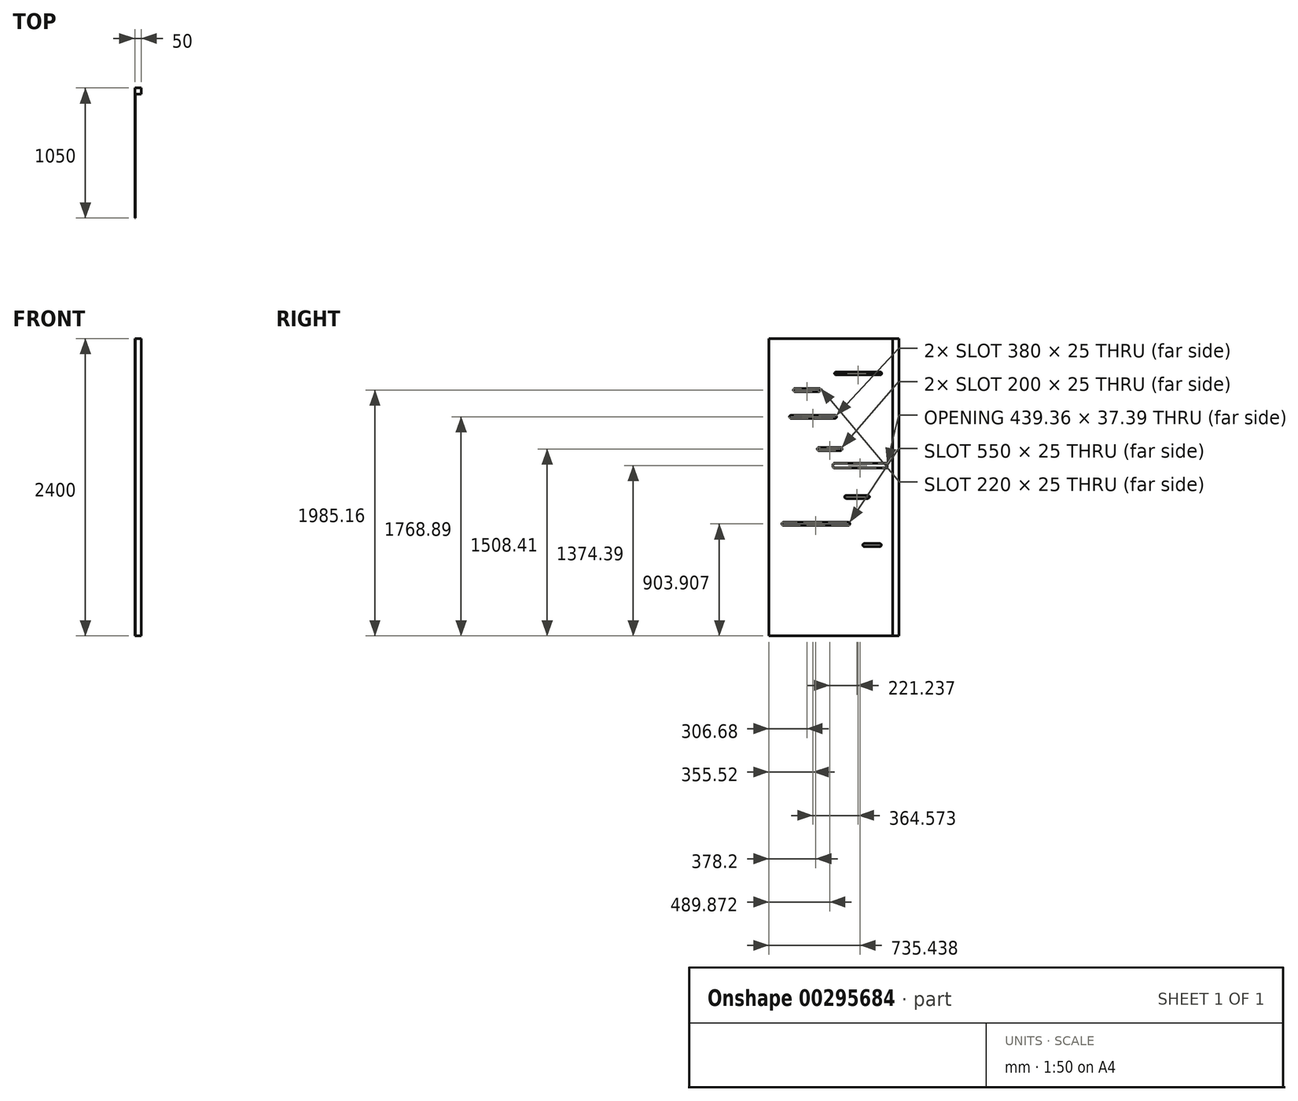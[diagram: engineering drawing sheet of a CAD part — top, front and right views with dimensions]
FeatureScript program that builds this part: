
annotation { "Feature Type Name" : "Feature", "Feature Type Description" : "" }
export const myFeature = defineFeature(function(context is Context, id is Id, definition is map)
    precondition{}
    {
        {
            var Q0;
            Q0=qCreatedBy(makeId("Top.planeOp"),FACE);
            var sketch = newSketch(context, id + "F0", { "sketchPlane" : qUnion([Q0])});
            skLineSegment(sketch, "E0.bottom", {"start": v(0, 0) * mm, "end": v(-50, 0) * mm});
            skLineSegment(sketch, "E0.top", {"start": v(0, -50) * mm, "end": v(-50, -50) * mm});
            skLineSegment(sketch, "E0.left", {"start": v(0, 0) * mm, "end": v(0, -50) * mm});
            skLineSegment(sketch, "E0.right", {"start": v(-50, 0) * mm, "end": v(-50, -50) * mm});
            skLineSegment(sketch, "E1.bottom", {"start": v(-50, -50) * mm, "end": v(-47, -50) * mm});
            skLineSegment(sketch, "E1.top", {"start": v(-50, -1050) * mm, "end": v(-47, -1050) * mm});
            skLineSegment(sketch, "E1.left", {"start": v(-50, -50) * mm, "end": v(-50, -1050) * mm});
            skLineSegment(sketch, "E1.right", {"start": v(-47, -50) * mm, "end": v(-47, -1050) * mm});
            skSolve(sketch);
        }
        {
            var Q0;
            Q0 = qSketchRegion(id + "F0", true);
            extrude(context, id + "F1", {"entities" : qUnion([Q0]), "depth" : 2400 * mm});
        }
        {
            var Q0;
            Q0=makeQuery(id+"F1.opExtrude","SWEPT_FACE",FACE,{"disambiguationData":[OSD([sQuery(id+"F0.wireOp",EDGE,"E0.right"),sQuery(id+"F0.wireOp",EDGE,"E1.left")])]});
            var sketch = newSketch(context, id + "F2", { "sketchPlane" : qUnion([Q0])});
            skLineSegment(sketch, "E2.bottom", {"start": v(152.4, 2131.65) * mm, "end": v(507.4, 2131.65) * mm});
            skLineSegment(sketch, "E2.top", {"start": v(152.4, 2106.65) * mm, "end": v(507.4, 2106.65) * mm});
            skLineSegment(sketch, "E2.left", {"start": v(139.9, 2119.15) * mm, "end": v(139.9, 2119.15) * mm});
            skLineSegment(sketch, "E2.right", {"start": v(519.9, 2119.15) * mm, "end": v(519.9, 2119.15) * mm});
            skLineSegment(sketch, "E3.bottom", {"start": v(516.98, 1781.39) * mm, "end": v(871.98, 1781.39) * mm});
            skLineSegment(sketch, "E3.top", {"start": v(516.98, 1756.39) * mm, "end": v(871.98, 1756.39) * mm});
            skLineSegment(sketch, "E3.left", {"start": v(504.48, 1768.89) * mm, "end": v(504.48, 1768.89) * mm});
            skLineSegment(sketch, "E3.right", {"start": v(884.48, 1768.89) * mm, "end": v(884.48, 1768.89) * mm});
            skLineSegment(sketch, "E4.bottom", {"start": v(472.63, 1520.91) * mm, "end": v(647.63, 1520.91) * mm});
            skLineSegment(sketch, "E4.top", {"start": v(472.63, 1495.91) * mm, "end": v(647.63, 1495.91) * mm});
            skLineSegment(sketch, "E4.left", {"start": v(460.13, 1508.41) * mm, "end": v(460.13, 1508.41) * mm});
            skLineSegment(sketch, "E4.right", {"start": v(660.13, 1508.41) * mm, "end": v(660.13, 1508.41) * mm});
            skLineSegment(sketch, "E5.bottom", {"start": v(251.4, 1134.53) * mm, "end": v(426.4, 1134.53) * mm});
            skLineSegment(sketch, "E5.top", {"start": v(251.4, 1109.53) * mm, "end": v(426.4, 1109.53) * mm});
            skLineSegment(sketch, "E5.left", {"start": v(238.9, 1122.03) * mm, "end": v(238.9, 1122.03) * mm});
            skLineSegment(sketch, "E5.right", {"start": v(438.9, 1122.03) * mm, "end": v(438.9, 1122.03) * mm});
            skLineSegment(sketch, "E6.bottom", {"start": v(409.3, 916.4) * mm, "end": v(934.3, 916.4) * mm});
            skLineSegment(sketch, "E6.top", {"start": v(409.3, 891.4) * mm, "end": v(934.3, 891.4) * mm});
            skLineSegment(sketch, "E6.left", {"start": v(396.8, 903.9) * mm, "end": v(396.8, 903.9) * mm});
            skLineSegment(sketch, "E6.right", {"start": v(946.8, 903.9) * mm, "end": v(946.8, 903.9) * mm});
            skLineSegment(sketch, "E7.bottom", {"start": v(154.94, 745.03) * mm, "end": v(279.94, 745.03) * mm});
            skLineSegment(sketch, "E7.top", {"start": v(154.94, 720.03) * mm, "end": v(279.94, 720.03) * mm});
            skLineSegment(sketch, "E7.left", {"start": v(142.44, 732.53) * mm, "end": v(142.44, 732.53) * mm});
            skLineSegment(sketch, "E7.right", {"start": v(292.44, 732.53) * mm, "end": v(292.44, 732.53) * mm});
            skLineSegment(sketch, "E8.bottom", {"start": v(645.82, 1997.66) * mm, "end": v(840.82, 1997.66) * mm});
            skLineSegment(sketch, "E8.top", {"start": v(645.82, 1972.66) * mm, "end": v(840.82, 1972.66) * mm});
            skLineSegment(sketch, "E8.left", {"start": v(633.32, 1985.16) * mm, "end": v(633.32, 1985.16) * mm});
            skLineSegment(sketch, "E8.right", {"start": v(853.32, 1985.16) * mm, "end": v(853.32, 1985.16) * mm});
            skPoint(sketch, "E9.visualSharp", {"position": v(504.48, 1781.39) * mm});
            skArc(sketch, "E9.filletArc", {"start": v(516.98, 1781.39) * mm, "mid": v(508.14, 1777.73) * mm, "end": v(504.48, 1768.89) * mm});
            skPoint(sketch, "E10.visualSharp", {"position": v(504.48, 1756.39) * mm});
            skArc(sketch, "E10.filletArc", {"start": v(504.48, 1768.89) * mm, "mid": v(508.14, 1760.05) * mm, "end": v(516.98, 1756.39) * mm});
            skPoint(sketch, "E11.visualSharp", {"position": v(884.48, 1781.39) * mm});
            skArc(sketch, "E11.filletArc", {"start": v(884.48, 1768.89) * mm, "mid": v(880.82, 1777.73) * mm, "end": v(871.98, 1781.39) * mm});
            skPoint(sketch, "E12.visualSharp", {"position": v(884.48, 1756.39) * mm});
            skArc(sketch, "E12.filletArc", {"start": v(871.98, 1756.39) * mm, "mid": v(880.82, 1760.05) * mm, "end": v(884.48, 1768.89) * mm});
            skPoint(sketch, "E13.visualSharp", {"position": v(660.13, 1520.91) * mm});
            skArc(sketch, "E13.filletArc", {"start": v(660.13, 1508.41) * mm, "mid": v(656.47, 1517.25) * mm, "end": v(647.63, 1520.91) * mm});
            skPoint(sketch, "E14.visualSharp", {"position": v(660.13, 1495.91) * mm});
            skArc(sketch, "E14.filletArc", {"start": v(647.63, 1495.91) * mm, "mid": v(656.47, 1499.57) * mm, "end": v(660.13, 1508.41) * mm});
            skPoint(sketch, "E15.visualSharp", {"position": v(460.13, 1495.91) * mm});
            skArc(sketch, "E15.filletArc", {"start": v(460.13, 1508.41) * mm, "mid": v(463.79, 1499.57) * mm, "end": v(472.63, 1495.91) * mm});
            skPoint(sketch, "E16.visualSharp", {"position": v(460.13, 1520.91) * mm});
            skArc(sketch, "E16.filletArc", {"start": v(472.63, 1520.91) * mm, "mid": v(463.79, 1517.25) * mm, "end": v(460.13, 1508.41) * mm});
            skPoint(sketch, "E17.visualSharp", {"position": v(853.32, 1997.66) * mm});
            skArc(sketch, "E17.filletArc", {"start": v(853.32, 1985.16) * mm, "mid": v(849.66, 1994) * mm, "end": v(840.82, 1997.66) * mm});
            skPoint(sketch, "E18.visualSharp", {"position": v(853.32, 1972.66) * mm});
            skArc(sketch, "E18.filletArc", {"start": v(840.82, 1972.66) * mm, "mid": v(849.66, 1976.32) * mm, "end": v(853.32, 1985.16) * mm});
            skPoint(sketch, "E19.visualSharp", {"position": v(438.9, 1134.53) * mm});
            skArc(sketch, "E19.filletArc", {"start": v(438.9, 1122.03) * mm, "mid": v(435.23, 1130.87) * mm, "end": v(426.4, 1134.53) * mm});
            skPoint(sketch, "E20.visualSharp", {"position": v(438.9, 1109.53) * mm});
            skArc(sketch, "E20.filletArc", {"start": v(426.4, 1109.53) * mm, "mid": v(435.23, 1113.19) * mm, "end": v(438.9, 1122.03) * mm});
            skPoint(sketch, "E21.visualSharp", {"position": v(238.9, 1134.53) * mm});
            skArc(sketch, "E21.filletArc", {"start": v(251.4, 1134.53) * mm, "mid": v(242.55, 1130.87) * mm, "end": v(238.9, 1122.03) * mm});
            skPoint(sketch, "E22.visualSharp", {"position": v(238.9, 1109.53) * mm});
            skArc(sketch, "E22.filletArc", {"start": v(238.9, 1122.03) * mm, "mid": v(242.55, 1113.19) * mm, "end": v(251.4, 1109.53) * mm});
            skPoint(sketch, "E23.visualSharp", {"position": v(396.8, 916.4) * mm});
            skArc(sketch, "E23.filletArc", {"start": v(409.3, 916.4) * mm, "mid": v(400.46, 912.75) * mm, "end": v(396.8, 903.9) * mm});
            skPoint(sketch, "E24.visualSharp", {"position": v(396.8, 891.4) * mm});
            skArc(sketch, "E24.filletArc", {"start": v(396.8, 903.9) * mm, "mid": v(400.46, 895.07) * mm, "end": v(409.3, 891.4) * mm});
            skPoint(sketch, "E25.visualSharp", {"position": v(946.8, 916.4) * mm});
            skArc(sketch, "E25.filletArc", {"start": v(946.8, 903.9) * mm, "mid": v(943.14, 912.75) * mm, "end": v(934.3, 916.4) * mm});
            skPoint(sketch, "E26.visualSharp", {"position": v(946.8, 891.4) * mm});
            skArc(sketch, "E26.filletArc", {"start": v(934.3, 891.4) * mm, "mid": v(943.14, 895.07) * mm, "end": v(946.8, 903.9) * mm});
            skPoint(sketch, "E27.visualSharp", {"position": v(292.44, 745.03) * mm});
            skArc(sketch, "E27.filletArc", {"start": v(292.44, 732.53) * mm, "mid": v(288.78, 741.37) * mm, "end": v(279.94, 745.03) * mm});
            skPoint(sketch, "E28.visualSharp", {"position": v(292.44, 720.03) * mm});
            skArc(sketch, "E28.filletArc", {"start": v(279.94, 720.03) * mm, "mid": v(288.78, 723.69) * mm, "end": v(292.44, 732.53) * mm});
            skPoint(sketch, "E29.visualSharp", {"position": v(142.44, 745.03) * mm});
            skArc(sketch, "E29.filletArc", {"start": v(154.94, 745.03) * mm, "mid": v(146.1, 741.37) * mm, "end": v(142.44, 732.53) * mm});
            skPoint(sketch, "E30.visualSharp", {"position": v(142.44, 720.03) * mm});
            skArc(sketch, "E30.filletArc", {"start": v(142.44, 732.53) * mm, "mid": v(146.1, 723.69) * mm, "end": v(154.94, 720.03) * mm});
            skPoint(sketch, "E31.visualSharp", {"position": v(139.9, 2131.65) * mm});
            skArc(sketch, "E31.filletArc", {"start": v(152.4, 2131.65) * mm, "mid": v(143.57, 2127.99) * mm, "end": v(139.9, 2119.15) * mm});
            skPoint(sketch, "E32.visualSharp", {"position": v(139.9, 2106.65) * mm});
            skArc(sketch, "E32.filletArc", {"start": v(139.9, 2119.15) * mm, "mid": v(143.57, 2110.31) * mm, "end": v(152.4, 2106.65) * mm});
            skPoint(sketch, "E33.visualSharp", {"position": v(519.9, 2131.65) * mm});
            skArc(sketch, "E33.filletArc", {"start": v(519.9, 2119.15) * mm, "mid": v(516.25, 2127.99) * mm, "end": v(507.4, 2131.65) * mm});
            skPoint(sketch, "E34.visualSharp", {"position": v(519.9, 2106.65) * mm});
            skArc(sketch, "E34.filletArc", {"start": v(507.4, 2106.65) * mm, "mid": v(516.25, 2110.31) * mm, "end": v(519.9, 2119.15) * mm});
            skPoint(sketch, "E35.visualSharp", {"position": v(633.32, 1997.66) * mm});
            skArc(sketch, "E35.filletArc", {"start": v(645.82, 1997.66) * mm, "mid": v(636.98, 1994) * mm, "end": v(633.32, 1985.16) * mm});
            skPoint(sketch, "E36.visualSharp", {"position": v(633.32, 1972.66) * mm});
            skArc(sketch, "E36.filletArc", {"start": v(633.32, 1985.16) * mm, "mid": v(636.98, 1976.32) * mm, "end": v(645.82, 1972.66) * mm});
            skLineSegment(sketch, "E37.bottom", {"start": v(107.38, 1393.08) * mm, "end": v(521.74, 1393.08) * mm});
            skLineSegment(sketch, "E37.top", {"start": v(94.88, 1355.7) * mm, "end": v(521.74, 1355.7) * mm});
            skLineSegment(sketch, "E37.left", {"start": v(94.88, 1380.58) * mm, "end": v(94.88, 1355.7) * mm});
            skLineSegment(sketch, "E37.right", {"start": v(534.24, 1380.58) * mm, "end": v(534.24, 1368.2) * mm});
            skPoint(sketch, "E38.visualSharp", {"position": v(94.88, 1393.08) * mm});
            skArc(sketch, "E38.filletArc", {"start": v(107.38, 1393.08) * mm, "mid": v(98.54, 1389.42) * mm, "end": v(94.88, 1380.58) * mm});
            skPoint(sketch, "E39.visualSharp", {"position": v(534.24, 1393.08) * mm});
            skArc(sketch, "E39.filletArc", {"start": v(534.24, 1380.58) * mm, "mid": v(530.58, 1389.42) * mm, "end": v(521.74, 1393.08) * mm});
            skPoint(sketch, "E40.visualSharp", {"position": v(534.24, 1355.7) * mm});
            skArc(sketch, "E40.filletArc", {"start": v(521.74, 1355.7) * mm, "mid": v(530.58, 1359.35) * mm, "end": v(534.24, 1368.2) * mm});
            skSolve(sketch);
        }
        {
            var Q0;
            Q0 = qSketchRegion(id + "F2", true);
            extrude(context, id + "F3", {"entities" : qUnion([Q0]), "operationType" : NewBodyOperationType.REMOVE, "oppositeDirection" : true, "depth" : 25 * mm});
        }
    });
